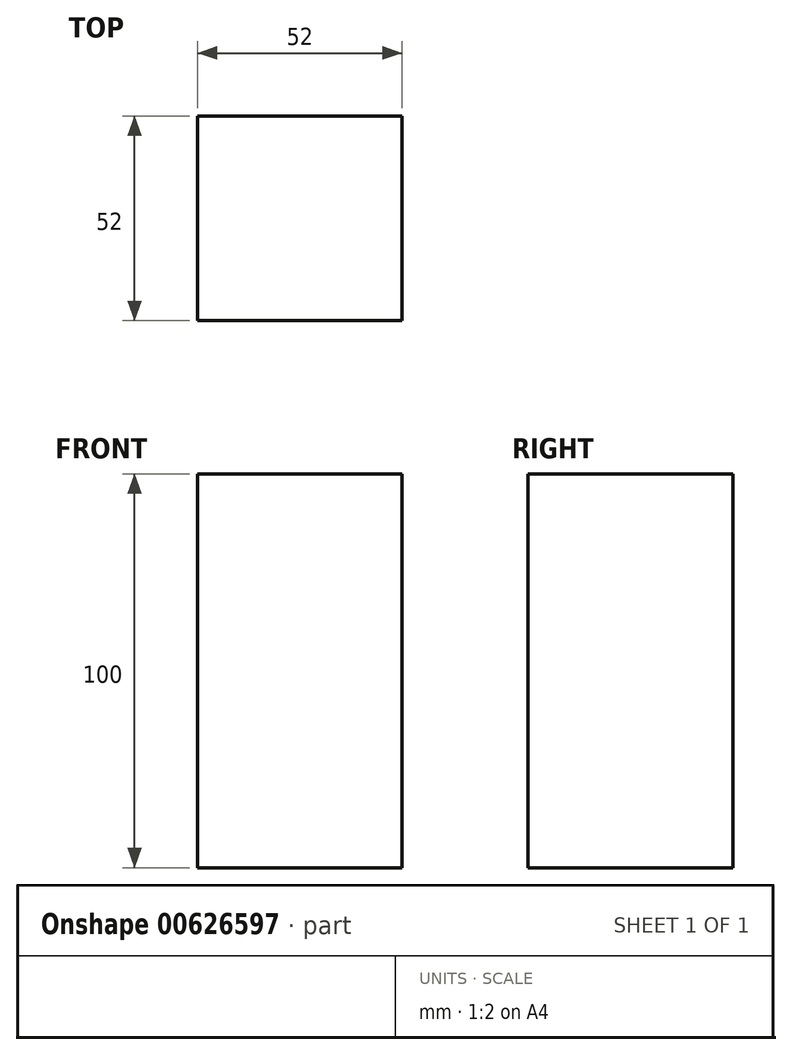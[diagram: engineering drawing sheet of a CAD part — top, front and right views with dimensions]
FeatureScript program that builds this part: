
annotation { "Feature Type Name" : "Feature", "Feature Type Description" : "" }
export const myFeature = defineFeature(function(context is Context, id is Id, definition is map)
    precondition{}
    {
        {
            var Q0;
            Q0=qCreatedBy(makeId("Top.planeOp"),FACE);
            var sketch = newSketch(context, id + "F0", { "sketchPlane" : qUnion([Q0])});
            skLineSegment(sketch, "E0.bottom", {"start": v(26, 26) * mm, "end": v(-26, 26) * mm});
            skLineSegment(sketch, "E0.top", {"start": v(26, -26) * mm, "end": v(-26, -26) * mm});
            skLineSegment(sketch, "E0.left", {"start": v(26, 26) * mm, "end": v(26, -26) * mm});
            skLineSegment(sketch, "E0.right", {"start": v(-26, 26) * mm, "end": v(-26, -26) * mm});
            skPoint(sketch, "E0.middle", {"position": v(0, 0) * mm});
            skSolve(sketch);
        }
        {
            var Q0;
            Q0=makeQuery(id+"F0.imprint","IMPRINT",FACE,{"disambiguationData":[TD([[makeQuery(id+"F0.imprint","IMPRINT",EDGE,{"derivedFrom":sQuery(id+"F0.wireOp",EDGE,"E0.bottom")}),1.0]])]});
            extrude(context, id + "F1", {"entities" : qUnion([Q0]), "depth" : 100 * mm});
        }
    });
